# Revit family: Mounting Brackets PNR-05554
name_source: partatom
category: Generic Models
revit_build: Autodesk Revit 2017 (Build: 20190508_0315(x64)
units: mm (PartAtom-declared; Revit-internal decimal feet)

## family parameters
Always vertical = No
Can host rebar = No
Cut with Voids When Loaded = No
Part Type = Normal
Room Calculation Point = No
Round Connector Dimension = Use Diameter
Shared = No
Work Plane-Based = Yes

## types (2) — shared parameters
Assembly Code = 63.0
Bolt_Material = Brass, Soft Yellow, Welded
Bolt_Visibility = No
Bracket Article Number = *User Defined
Bracket_Width = 15 mm  [stored 0.0492126 ft]
Default Elevation = 1219 mm
Description = Mounting Brackets
Find - Bracket Article Number = https://www.veko.com
Manufacturer = Veko Lightsystems
Mounting_Material = Aluminum 7175 T73 0 Hot Formed
Pendulum Visiblity = No

## per-type parameters (varying)
| type | B2-R | B2-SO-R | Pendulum Start |
| B2-R | Yes | No | 127 mm |
| B2-SO-R | No | Yes | 147 mm |

note: column(s) folded — value = type name in every type: Model

note: [stored X ft] marks values corroborated as IEEE doubles in the binary element streams (Revit-internal decimal feet)

## geometry (parser evidence)
native form markers: Sweep x2
no freeform markers — native parametric forms only
